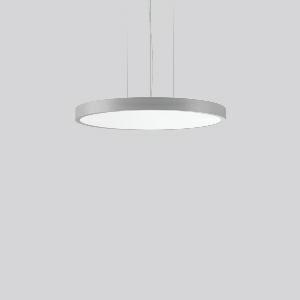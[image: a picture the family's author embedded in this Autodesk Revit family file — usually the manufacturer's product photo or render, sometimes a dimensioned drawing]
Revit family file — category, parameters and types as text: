
# Revit family: triona_round_p_312386_004_730_d534
name_source: partatom
category: Lighting Fixtures
units: mm (PartAtom-declared; Revit-internal decimal feet)

## family parameters
Cut with Voids When Loaded = No
Host = Face
Light Source = No
Part Type = Normal
Room Calculation Point = No
Round Connector Dimension = Use Diameter
Shared = No

## types (1)
- TRIONA round P (1 x LED Modul 830, 9300 lm, 3000)
    Apparent Load = 106 VA
    CIE Flux Codes = 49 80 96 72 100
    Color Rendering = 80
    Color Temperature = 3000
    Default Elevation = 1800 mm
    Description = Series: TRIONA round
Decorative round LED pendant-mounted surface luminaire. Flat, seamless frame: aluminium extrusion profile, powder coated. Cover made of sheet steel, powder-coated. Canopy made of aluminium, powder-coated. Direct light emission through a diffuser plastic opal. Indirect light emission through a flush diffuser made of satin-finish plastic. Lightguide and diffuser made of non-yellowing plastic (PMMA). Lateral light emission (RZB SIDELITE technology) for above-average homogeneous light distribution. Direct 70%, indirect 30% light emission. 3-point steel cable suspension, steplessly adjustable. Easy installation with transparent, adjustable pendant cable and canopy with magnetic fixing. Driver integrated. 
Colour: silver, matt (approx. RAL 9006)
Diameter: 681 mm
Height: 52 mm
Suspension length: 500-1200 mm
Lamp: LED
Socket: without socket
Colour temperature: 3000K
Colour rendering index (CRI): 80
System power: 106 W
Rated luminous flux: 9300 lm
Luminous efficiency: 88 lm/W
Control gear: Dimmable Bluetooth converter
Protection class: I
Type of protection: IP 20
    Height = 52 mm  [stored 0.170604 ft]
    Lamp = 1 x LED Modul 830
    Lamp Light Flux = 9300 lm
    Lamp count = 1
    Length = 681 mm
    Lifetime = 50000 h
    Luminous efficacy = 88 lm/W
    Manufacturer = RZB
    ModVariant = No
    Model = 312386.004.730
    Mounting Place = Ceiling
    Mounting Type = Pendant
    Number of Poles = 1
    OnlyDefault = Yes
    Power Factor = 1
    Product Name = TRIONA round P
    Product group = Pendant modular luminaires
    ProductGroupID = 906
    Protection Class = Protection class I
    Protection Degree = IP 20
    RLX_Detail_Level = 1
    RLX_Emergency_Light_Flux = 0 lm
    RLX_Emergency_Type = 0
    RLX_Emergency_Type_DB = No
    RlxData = <blob elided: 38609 chars, md5=680b67d0>
    Socket = socket
    Standby Power = 0 W
    System Light Flux = 9300 lm
    System Power = 106 W
    Type Comments = Product without accessories
    Type Image = 312386.004.jpg
    URL = http://relux.com
    VarID = ---
    Voltage = 230 V
    Voltage Range = 220-240 V
    Weight = 0.00 kg
    Width = 0 mm  [stored 0 ft]

note: [stored X ft] marks values corroborated as IEEE doubles in the binary element streams (Revit-internal decimal feet)

## geometry (parser evidence)
native form markers: Blend x4, Sweep x15
no freeform markers — native parametric forms only
